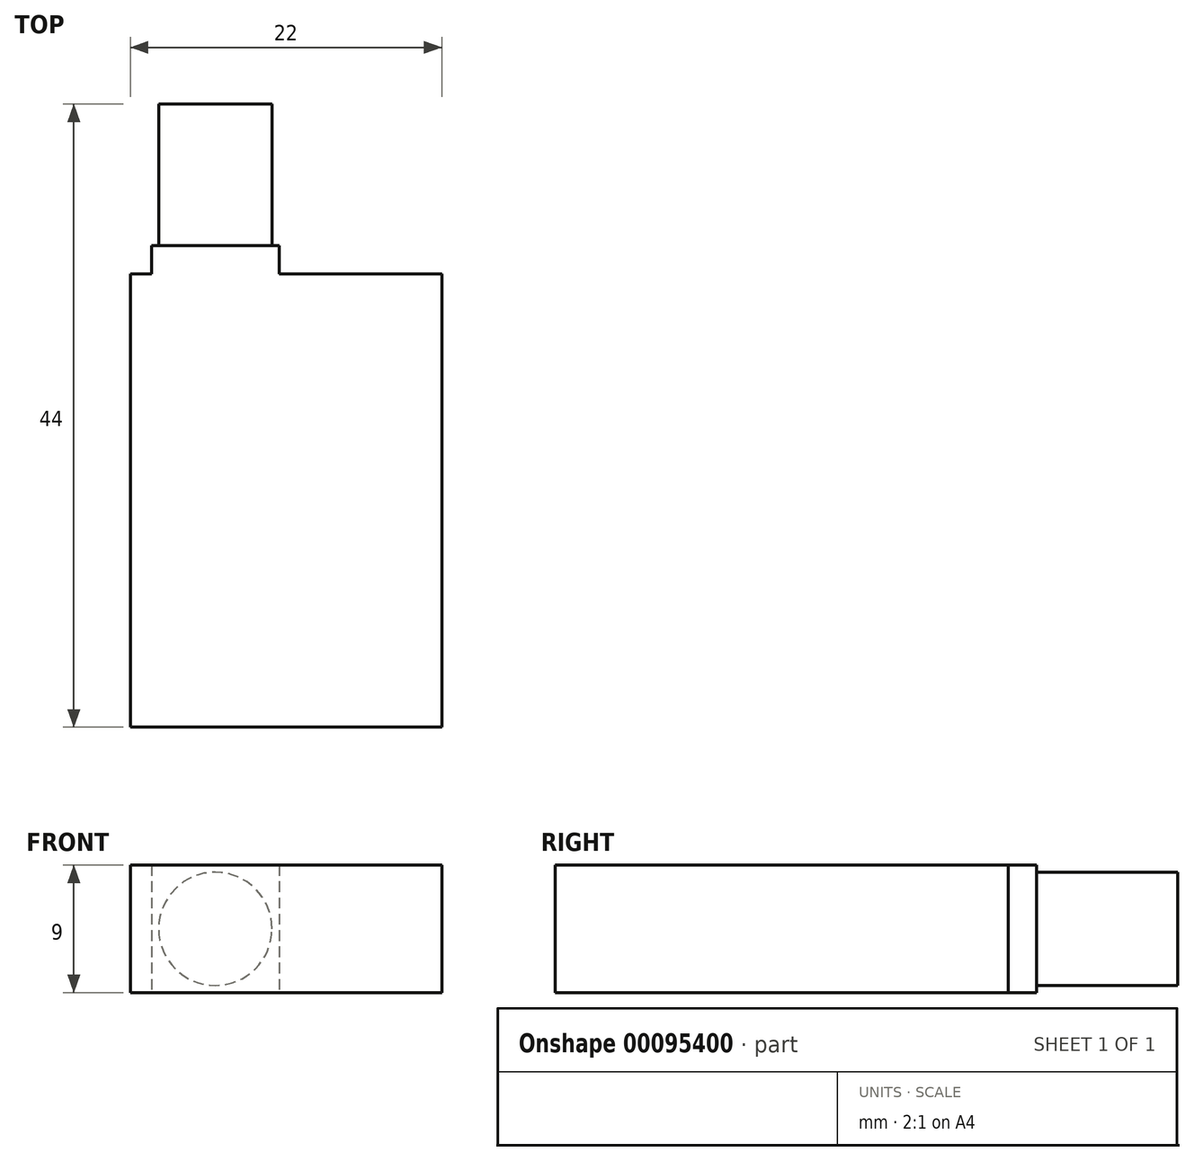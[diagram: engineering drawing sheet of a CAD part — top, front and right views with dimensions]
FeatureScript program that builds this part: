
annotation { "Feature Type Name" : "Feature", "Feature Type Description" : "" }
export const myFeature = defineFeature(function(context is Context, id is Id, definition is map)
    precondition{}
    {
        {
            var Q0;
            Q0=qCreatedBy(makeId("Top.planeOp"),FACE);
            var sketch = newSketch(context, id + "F0", { "sketchPlane" : qUnion([Q0])});
            skLineSegment(sketch, "E0.bottom", {"start": v(0, 0) * mm, "end": v(22, 0) * mm});
            skLineSegment(sketch, "E0.top", {"start": v(0, 32) * mm, "end": v(22, 32) * mm});
            skLineSegment(sketch, "E0.left", {"start": v(0, 0) * mm, "end": v(0, 32) * mm});
            skLineSegment(sketch, "E0.right", {"start": v(22, 0) * mm, "end": v(22, 32) * mm});
            skSolve(sketch);
        }
        {
            var Q0;
            Q0 = qSketchRegion(id + "F0", true);
            extrude(context, id + "F1", {"entities" : qUnion([Q0]), "depth" : 9 * mm});
        }
        {
            var Q0;
            Q0=makeQuery(id+"F1.opExtrude","SWEPT_FACE",FACE,{"disambiguationData":[OSD([sQuery(id+"F0.wireOp",EDGE,"E0.top")])]});
            var sketch = newSketch(context, id + "F2", { "sketchPlane" : qUnion([Q0])});
            skLineSegment(sketch, "E1.bottom", {"start": v(-1.5, 9) * mm, "end": v(-10.5, 9) * mm});
            skLineSegment(sketch, "E1.top", {"start": v(-1.5, 0) * mm, "end": v(-10.5, 0) * mm});
            skLineSegment(sketch, "E1.left", {"start": v(-1.5, 9) * mm, "end": v(-1.5, 0) * mm});
            skLineSegment(sketch, "E1.right", {"start": v(-10.5, 9) * mm, "end": v(-10.5, 0) * mm});
            skSolve(sketch);
        }
        {
            var Q0;
            Q0 = qSketchRegion(id + "F2", true);
            extrude(context, id + "F3", {"entities" : qUnion([Q0]), "operationType" : NewBodyOperationType.ADD, "depth" : 2 * mm});
        }
        {
            var Q0;
            Q0=makeQuery(id+"F3.opExtrude","CAP_FACE",FACE,{"disambiguationData":[OSD([sQuery(id+"F2.wireOp",EDGE,"E1.bottom"),sQuery(id+"F2.wireOp",EDGE,"E1.top"),sQuery(id+"F2.wireOp",EDGE,"E1.left"),sQuery(id+"F2.wireOp",EDGE,"E1.right")])],"isStart":false});
            var sketch = newSketch(context, id + "F4", { "sketchPlane" : qUnion([Q0])});
            skCircle(sketch, "E2", {"center": v(-6, 4.5) * mm, "radius": 4 * mm});
            skSolve(sketch);
        }
        {
            var Q0;
            Q0 = qSketchRegion(id + "F4", true);
            extrude(context, id + "F5", {"entities" : qUnion([Q0]), "operationType" : NewBodyOperationType.ADD, "depth" : 10 * mm});
        }
    });
